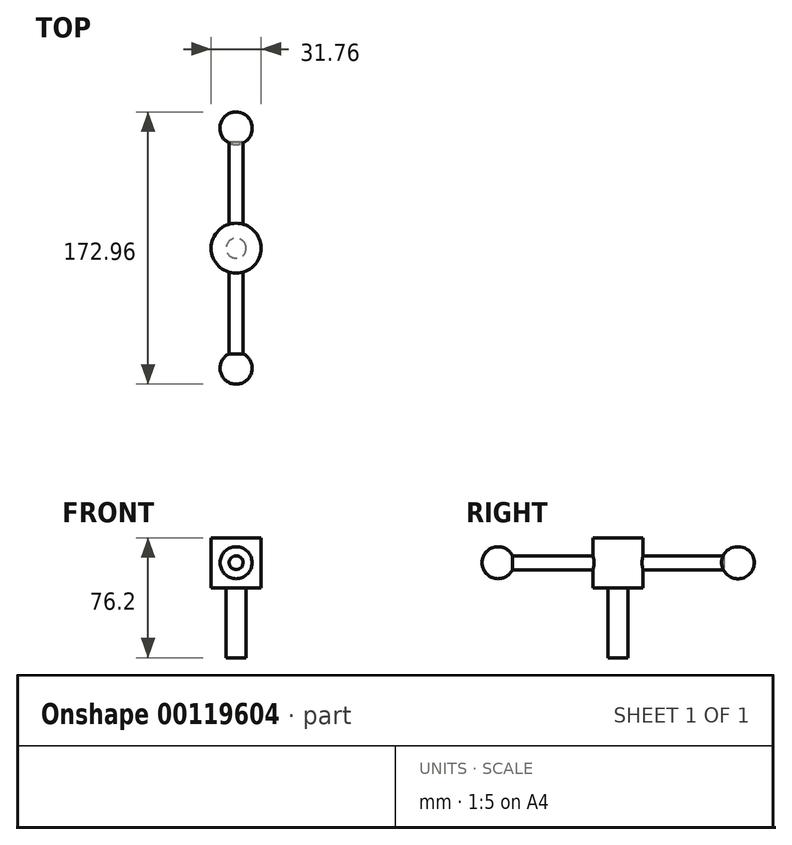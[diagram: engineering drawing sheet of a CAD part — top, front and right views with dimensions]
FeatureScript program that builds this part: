
annotation { "Feature Type Name" : "Feature", "Feature Type Description" : "" }
export const myFeature = defineFeature(function(context is Context, id is Id, definition is map)
    precondition{}
    {
        {
            var Q0;
            Q0=qCreatedBy(makeId("Top.planeOp"),FACE);
            var sketch = newSketch(context, id + "F0", { "sketchPlane" : qUnion([Q0])});
            skCircle(sketch, "E0", {"center": v(0, 0) * mm, "radius": 15.88 * mm});
            skSolve(sketch);
        }
        {
            var Q0;
            Q0 = qSketchRegion(id + "F0", true);
            extrude(context, id + "F1", {"entities" : qUnion([Q0]), "depth" : 31.75 * mm});
        }
        {
            var Q0;
            Q0=makeQuery(id+"F1.opExtrude","CAP_FACE",FACE,{"disambiguationData":[OSD([sQuery(id+"F0.wireOp",EDGE,"E0")])],"isStart":true});
            var sketch = newSketch(context, id + "F2", { "sketchPlane" : qUnion([Q0])});
            skCircle(sketch, "E1", {"center": v(0, 0) * mm, "radius": 6.35 * mm});
            skSolve(sketch);
        }
        {
            var Q0;
            Q0 = qSketchRegion(id + "F2", true);
            extrude(context, id + "F3", {"entities" : qUnion([Q0]), "operationType" : NewBodyOperationType.ADD, "depth" : 44.45 * mm});
        }
        {
            var Q0;
            Q0=qCreatedBy(makeId("Right.planeOp"),FACE);
            var sketch = newSketch(context, id + "F4", { "sketchPlane" : qUnion([Q0])});
            skLineSegment(sketch, "E2", {"start": v(0, 15.88) * mm, "end": v(76.2, 15.88) * mm});
            skLineSegment(sketch, "E3", {"start": v(0, 15.88) * mm, "end": v(0, 0) * mm, "construction": true});
            skSolve(sketch);
        }
        {
            var Q0;
            Q0=qCreatedBy(makeId("Front.planeOp"),FACE);
            var sketch = newSketch(context, id + "F5", { "sketchPlane" : qUnion([Q0])});
            skLineSegment(sketch, "E4", {"start": v(0, 0) * mm, "end": v(0, 15.87) * mm, "construction": true});
            skCircle(sketch, "E5", {"center": v(0, 15.87) * mm, "radius": 4.45 * mm});
            skSolve(sketch);
        }
        {
            var Q0;
            Q0 = qSketchRegion(id + "F5", true);
            extrude(context, id + "F6", {"entities" : qUnion([Q0]), "operationType" : NewBodyOperationType.ADD, "depth" : 76.2 * mm, "hasSecondDirection" : true, "secondDirectionOppositeDirection" : true, "secondDirectionDepth" : 76.2 * mm});
        }
        {
            var Q0;
            Q0=qCreatedBy(makeId("Right.planeOp"),FACE);
            var sketch = newSketch(context, id + "F7", { "sketchPlane" : qUnion([Q0])});
            skArc(sketch, "E6", {"start": v(76.2, 5.7) * mm, "mid": v(86.12, 15.86) * mm, "end": v(76.2, 26.02) * mm});
            skLineSegment(sketch, "E7", {"start": v(76.2, 26.02) * mm, "end": v(76.2, 5.7) * mm});
            skLineSegment(sketch, "E8", {"start": v(0, 0) * mm, "end": v(0, 15.87) * mm, "construction": true});
            skLineSegment(sketch, "E9", {"start": v(0, 15.87) * mm, "end": v(-76.2, 15.87) * mm, "construction": true});
            skArc(sketch, "E10", {"start": v(-76.2, 26.03) * mm, "mid": v(-86.36, 15.87) * mm, "end": v(-76.2, 5.71) * mm});
            skLineSegment(sketch, "E11", {"start": v(-76.2, 26.04) * mm, "end": v(-76.2, 5.71) * mm});
            skSolve(sketch);
        }
        {
            var Q0;
            Q0=makeQuery(id+"F7.imprint","IMPRINT",FACE,{"disambiguationData":[TD([[makeQuery(id+"F7.imprint","IMPRINT",EDGE,{"derivedFrom":sQuery(id+"F7.wireOp",EDGE,"E6")}),1.0]])]});
            var Q1;
            Q1=sQuery(id+"F7.wireOp",EDGE,"E7");
            revolve(context, id + "F8", {"operationType" : NewBodyOperationType.ADD, "entities" : qUnion([Q0]), "axis" : qUnion([Q1]), "revolveType" : RevolveType.FULL});
        }
        {
            var Q0;
            Q0=makeQuery(id+"F7.imprint","IMPRINT",FACE,{"disambiguationData":[TD([[makeQuery(id+"F7.imprint","IMPRINT",EDGE,{"derivedFrom":sQuery(id+"F7.wireOp",EDGE,"E10")}),1.0]])]});
            var Q1;
            Q1=sQuery(id+"F7.wireOp",EDGE,"E10");
            var Q2;
            Q2=sQuery(id+"F7.wireOp",EDGE,"E11");
            revolve(context, id + "F9", {"operationType" : NewBodyOperationType.ADD, "entities" : qUnion([Q0]), "surfaceEntities" : qUnion([Q1]), "axis" : qUnion([Q2]), "revolveType" : RevolveType.FULL});
        }
    });
